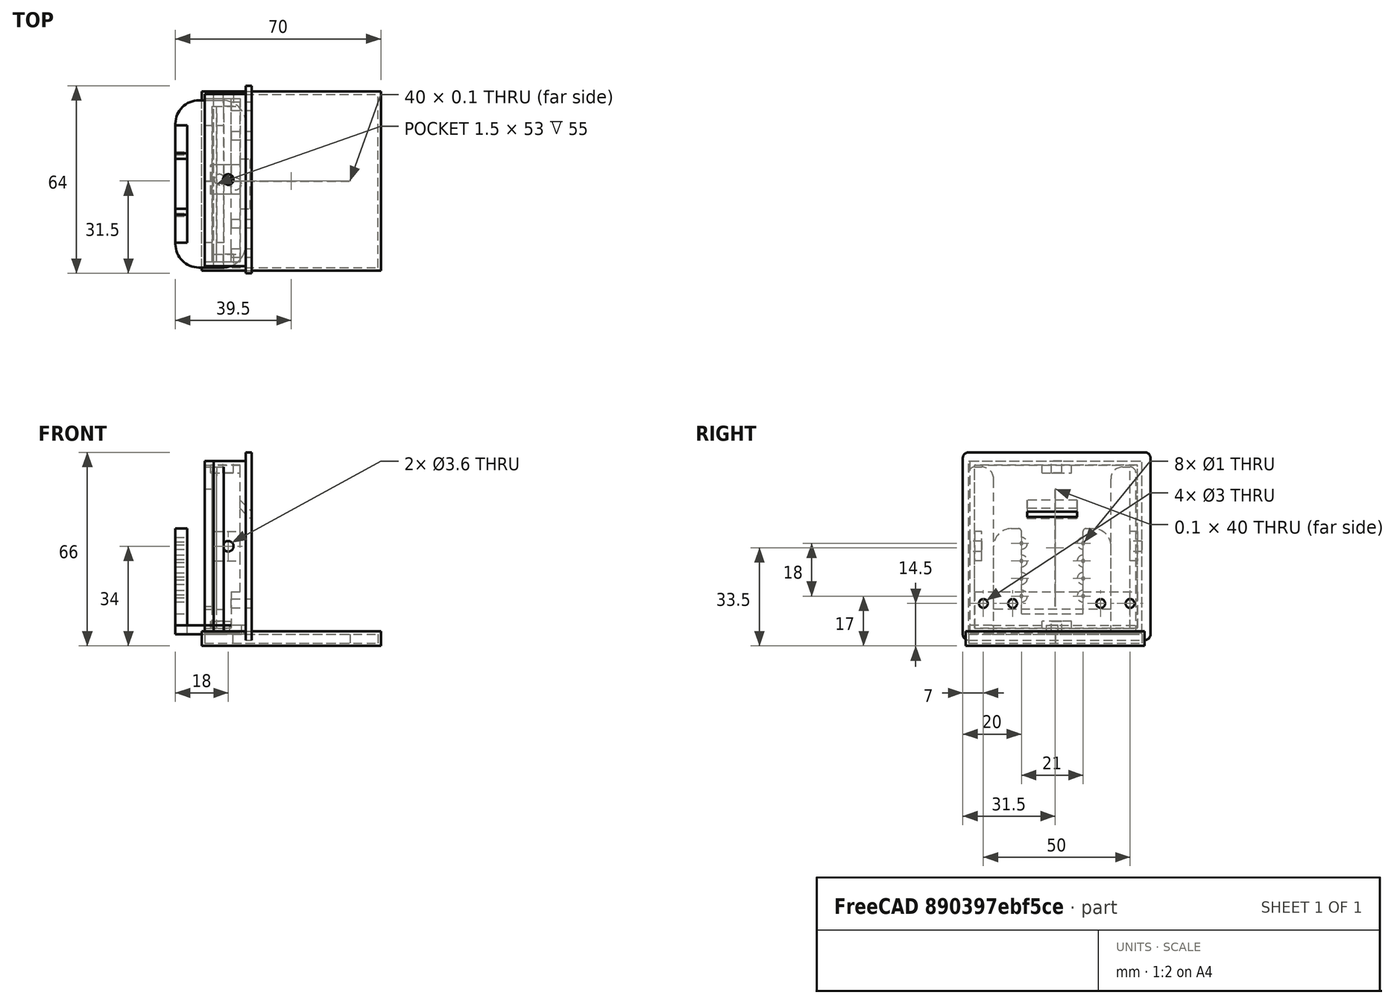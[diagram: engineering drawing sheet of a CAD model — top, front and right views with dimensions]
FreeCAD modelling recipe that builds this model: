
FCSTD DOCUMENT  (FreeCAD 0.18.4R)
Label: spectrometer
License: All rights reserved
LicenseURL: http://en.wikipedia.org/wiki/All_rights_reserved
objects: Part::Box×15, Part::FeaturePython×8, Part::Cylinder×7, Part::Cut×7, App::Part×6, Part::MultiFuse×6, Part::Fillet×6, Part::Feature×6, Path::FeaturePython×4, Spreadsheet::Sheet×1, Part::Compound×1, App::FeaturePython×1, App::DocumentObjectGroup×1, Path::FeatureCompoundPython×1, Part::Mirroring×1
note: 58 computed .brp shape members not serialized (recipe doc carries the construction recipe); baked Part::Feature solids carry a one-line shape summary decoded from their .brp

FEATURE [App::Part] Part  label="slide holder part"
  Origin = -> Origin
FEATURE [App::Part] Part001  label="rpi camera holder part"
  Origin = -> Origin001
FEATURE [Part::Cylinder] Cylinder  label="camera hole base"
  Angle = 360
  AttacherType = Attacher::AttachEngine3D
  Height = 4
  Placement = pos=(0,0,0) rot=(0,1,0;1.5708rad)
  Radius = 2
FEATURE [Part::FeaturePython] Array  label="camera hole base array"  # Draft array (typed FeaturePython)
  Angle = 360
  ArrayType = 0
  Axis = (0,0,1)
  Base = -> Cylinder
  Center = (0,0,0)
  Fuse = false
  IntervalAxis = (0,0,0)
  IntervalX = (1,0,0)
  IntervalY = (0,21,0)
  IntervalZ = (0,0,6)
  NumberPolar = 1
  NumberX = 1
  NumberY = 2
  NumberZ = 4
  Placement = pos=(0,7,2) rot=(0,0,1;0rad)
  expr: IntervalZ.z = p.camera_hole_dist_z / 2
  expr: IntervalY.y = p.camera_hole_dist_y
FEATURE [Spreadsheet::Sheet] Spreadsheet  label="p"
  cells = A1=camera_pcb_width; B1(camera_pcb_width)=25; A2=camera_pcb_height; B2(camera_pcb_height)=24; A3=camera_hole_dist_z; B3(camera_hole_dist_z)=12; A4=camera_hole_dist_y; B4(camera_hole_dist_y)=21; A5=slit_plate_width; B5(slit_plate_width)=59; A6=slit_plate_height; B6(slit_plate_height)=59; A7=slit_hole_height; B7(slit_hole_height)=40; A8=slit_hole_width; B8(slit_hole_width)=0.1
FEATURE [Part::Cylinder] Cylinder001  label="camera hole"
  Angle = 360
  AttacherType = Attacher::AttachEngine3D
  Height = 4
  Placement = pos=(0,0,0) rot=(0,1,0;1.5708rad)
  Radius = 0.5
FEATURE [Part::FeaturePython] Array001  label="camera hole array"  # Draft array (typed FeaturePython)
  Angle = 360
  ArrayType = 0
  Axis = (0,0,1)
  Base = -> Cylinder001
  Center = (0,0,0)
  Fuse = false
  IntervalAxis = (0,0,0)
  IntervalX = (1,0,0)
  IntervalY = (0,21,0)
  IntervalZ = (0,0,6)
  NumberPolar = 1
  NumberX = 1
  NumberY = 2
  NumberZ = 4
  Placement = pos=(0,7,2) rot=(0,0,1;0rad)
  expr: IntervalZ.z = p.camera_hole_dist_z / 2
  expr: IntervalY.y = p.camera_hole_dist_y
FEATURE [Part::Box] Box  label="camera plate"
  AttacherType = Attacher::AttachEngine3D
  Height = 36
  Length = 4
  Placement = pos=(0,-2.5,-11) rot=(0,0,1;0rad)
  Width = 40
FEATURE [Part::Box] Box001  label="camera plate hole"
  AttacherType = Attacher::AttachEngine3D
  Height = 74
  Length = 4
  Placement = pos=(0,7,-4) rot=(0,0,1;0rad)
  Width = 21
  expr: Height = p.camera_pcb_height + 50
  expr: Width = p.camera_pcb_width - 4
FEATURE [Part::Box] Box002  label="slide holder"
  AttacherType = Attacher::AttachEngine3D
  Height = 57
  Length = 6.5
  Width = 57
FEATURE [Part::Box] Box003  label="slide hole"
  AttacherType = Attacher::AttachEngine3D
  Height = 80
  Length = 1.5
  Placement = pos=(2.5,2,2) rot=(0,0,1;0rad)
  Width = 53
FEATURE [Part::Box] Box004  label="slide holder central hole"
  AttacherType = Attacher::AttachEngine3D
  Height = 100
  Length = 10
  Placement = pos=(-2,8.5,8.5) rot=(0,0,1;0rad)
  Width = 40
FEATURE [Part::MultiFuse] Fusion001  label="slide holder hole fusion"
  Shapes = -> [Box003,Box004]
FEATURE [Part::Box] Box005  label="bottom plate"
  AttacherType = Attacher::AttachEngine3D
  Height = 3
  Length = 24
  Placement = pos=(-10,0,0) rot=(0,0,1;0rad)
  Width = 57
FEATURE [Part::Cylinder] Cylinder002  label="central bottom hole"
  Angle = 360
  AttacherType = Attacher::AttachEngine3D
  Height = 10
  Placement = pos=(10.5,28.5,-4) rot=(0,0,1;0rad)
  Radius = 2
FEATURE [Part::Fillet] Fillet  label="bottom plate fillet"
  Base = -> Box005
  Edges = 4 edges r=8: [Edge1,Edge3,Edge5,Edge7]
FEATURE [Part::Cut] Cut003  label="bottom cut"
  Base = -> Fillet
  Tool = -> Cylinder002
FEATURE [Part::Fillet] Fillet001  label="camera plate fillet"
  Base = -> Box
  Edges = 2 edges r=6: [Edge10,Edge12]
FEATURE [Part::Cut] Cut001  label="camera plate cut"
  Base = -> Fillet001
  Tool = -> Box001
FEATURE [Part::Fillet] Fillet002  label="slide holder fillet"
  Base = -> Box002
  Edges = 2 edges r=2: [Edge10,Edge12]
FEATURE [Part::Cut] Cut002  label="slide holder cut"
  Base = -> Fillet002
  Tool = -> Fusion001
FEATURE [Part::Fillet] Fillet003  label="slider holder cut fillet"
  Base = -> Cut002
  Edges = 4 edges r=4: [Edge16,Edge23,Edge39,Edge49]
FEATURE [Part::Fillet] Fillet004  label="camera plate cut fillet"
  Base = -> Cut001
  Edges = 2 edges r=1: [Edge14,Edge21]
FEATURE [Part::MultiFuse] Fusion  label="camera plate fusion"
  Shapes = -> [Array,Fillet004]
FEATURE [Part::Cut] Cut  label="camera holder cut"
  Base = -> Fusion
  Placement = pos=(-10,11,11) rot=(0,0,1;0rad)
  Tool = -> Array001
FEATURE [Part::Compound] Compound  label="rpi camera slide holder"
  Links = -> [Cut003,Fillet003,Cut]
FEATURE [App::Part] Part002  label="bottom part"
  Group = -> [Box005,Cylinder002,Cut003,Fillet,Array,Compound,Fusion001,Fusion,Cut002,Cut,Cut001,Fillet002,Array001,Fillet001,Cylinder,Cylinder001,Box,Box001,Box002,Box003,Box004,Fillet003,Fillet004]
  Origin = -> Origin002
FEATURE [Part::Box] Box006  label="slit plate"
  AttacherType = Attacher::AttachEngine3D
  Height = 59
  Length = 3
  Width = 59
  expr: Height = p.slit_plate_height
  expr: Width = p.slit_plate_width
FEATURE [Part::Box] Box007  label="slit hole"
  AttacherType = Attacher::AttachEngine3D
  Height = 40
  Length = 10
  Placement = pos=(-3,29.45,9.5) rot=(0,0,1;0rad)
  Width = 0.1
  expr: Placement.Base.y = (p.slit_plate_width - p.slit_hole_width) / 2
  expr: Placement.Base.z = (p.slit_plate_height - p.slit_hole_height) / 2
  expr: Height = p.slit_hole_height
  expr: Width = p.slit_hole_width
FEATURE [Part::Cut] Cut004  label="slit plate cut"
  Base = -> Box006
  Tool = -> Box007
FEATURE [App::Part] Part003  label="slit part"
  Group = -> [Box006,Box007,Cut004]
  Origin = -> Origin003
  Placement = pos=(-125,-29,3) rot=(0,0,1;0rad)
FEATURE [Part::Feature] Cut004001  label="slit plate refine"
  Placement = pos=(0,0,0) rot=(0,1,0;1.5708rad)
  shape: bbox 59 x 59 x 3 mm, 10 faces (baked)
FEATURE [App::FeaturePython] SetupSheet  # Path/CAM operation (typed FeaturePython)
  ClearanceHeightExpression = OpStockZMax+SetupSheet.ClearanceHeightOffset
  ClearanceHeightOffset = 0
  FinalDepthExpression = OpFinalDepth
  HorizRapid = 100
  SafeHeightExpression = OpStockZMax+SetupSheet.SafeHeightOffset
  SafeHeightOffset = 0
  StartDepthExpression = OpStartDepth
  StepDownExpression = OpToolDiameter
  VertRapid = 100
FEATURE [Part::FeaturePython] Clone  label="Model-slit plate refine"  # Draft clone (typed FeaturePython)
  AttacherType = Attacher::AttachEngine3D
  Fuse = false
  Objects = -> [Cut004001]
  PathResource = Model
  Placement = pos=(0,0,0) rot=(0,1,0;1.5708rad)
  Scale = (1,1,1)
FEATURE [App::DocumentObjectGroup] Model
  Group = -> [Clone]
FEATURE [Path::FeaturePython] T3__laser  label="T3: laser"  # Path/CAM operation (typed FeaturePython)
  HorizFeed = 0.5
  HorizRapid = 100
  SpindleDir = 0
  SpindleSpeed = 1000
  ToolNumber = 3
  VertFeed = 0.5
  VertRapid = 100
  expr: VertRapid = SetupSheet.VertRapid
  expr: HorizRapid = SetupSheet.HorizRapid
FEATURE [Part::FeaturePython] Stock  # WARN: FeaturePython — macro-defined, semantics opaque (R4)
  Base = -> Model
  ExtXneg = 1
  ExtXpos = 1
  ExtYneg = 1
  ExtYpos = 1
  ExtZneg = 1
  ExtZpos = 1
  Placement = pos=(0,0,-3) rot=(0,0,1;0rad)
  StockType = FromBase
FEATURE [Path::FeaturePython] Engrave  # Path/CAM operation (typed FeaturePython)
  Active = true
  Base = -> [Clone]
  ClearanceHeight = 1
  FinalDepth = 0
  OpFinalDepth = -0.2
  OpStartDepth = 1.31e-14
  OpStockZMax = 1
  OpStockZMin = -4
  OpToolDiameter = 0.2
  SafeHeight = 1
  StartDepth = 0.1
  StartVertex = 0
  StepDown = 0.2
  ToolController = -> T3__laser
  expr: ClearanceHeight = OpStockZMax + SetupSheet.ClearanceHeightOffset
  expr: SafeHeight = OpStockZMax + SetupSheet.SafeHeightOffset
  expr: StepDown = OpToolDiameter
FEATURE [Path::FeaturePython] Contour  # Path/CAM operation (typed FeaturePython)
  Active = true
  AreaParams:
    Tolerance = 1e-07
    FitArcs = True
    Simplify = False
    CleanDistance = 0.0
    Accuracy = 0.01
    Unit = 1.0
    MinArcPoints = 4
    MaxArcPoints = 100
    ClipperScale = 10000000.0
    Fill = 0
    Coplanar = 2
    Reorient = True
    Outline = False
    Explode = False
    OpenMode = 0
    Deflection = 0.01
    SubjectFill = 0
    ClipFill = 0
    Offset = 0.1
    ExtraPass = 0
    Stepover = 0.0
    LastStepover = 0.0
    JoinType = 0
    EndType = 0
    MiterLimit = 2.0
    RoundPrecision = 0.0
    PocketMode = 0
    ToolRadius = 1.0
    PocketExtraOffset = 0.0
    PocketStepover = 0.0
    PocketLastStepover = 0.0
    FromCenter = False
    Angle = 45.0
    AngleShift = 0.0
    Shift = 0.0
    Thicken = False
    SectionCount = -1
    Stepdown = 1.0
    SectionOffset = 0.0
    SectionTolerance = 1e-06
    SectionMode = 2
    Project = False
  ClearanceHeight = 1
  Direction = 0
  FinalDepth = 0
  JoinType = 0
  MiterLimit = 0.1
  OffsetExtra = 0
  OpFinalDepth = -4
  OpStartDepth = 1
  OpStockZMax = 1
  OpStockZMin = -4
  OpToolDiameter = 0.2
  PathParams = {'orientation': 1, 'feedrate': 0.5, 'feedrate_v': 0.5, 'verbose': True, 'resume_height': 1.0000000000000133, 'retraction': 1.0000000000000133, 'return_end': True, 'preamble': False}
  SafeHeight = 1
  Side = 0
  StartDepth = 0.1
  StartPoint = (0,0,0)
  StepDown = 0.2
  ToolController = -> T3__laser
  UseComp = true
  UseStartPoint = false
  expr: ClearanceHeight = OpStockZMax + SetupSheet.ClearanceHeightOffset
  expr: SafeHeight = OpStockZMax + SetupSheet.SafeHeightOffset
  expr: StepDown = OpToolDiameter
FEATURE [Path::FeatureCompoundPython] Operations  # Path/CAM operation (typed FeaturePython)
  Group = -> [Engrave,Contour]
  UsePlacements = false
FEATURE [Path::FeaturePython] Job  label="slit plate job"  # Path/CAM operation (typed FeaturePython)
  GeometryTolerance = 0.01
  Model = -> Model
  Operations = -> Operations
  PostProcessor = 1
  PostProcessorOutputFile = <userpath>/work/roborep/freecad/spectrometer/slit_plate.gcode
  SetupSheet = -> SetupSheet
  Stock = -> Stock
  ToolController = -> [T3__laser]
FEATURE [Part::Box] Box008  label="outer wall"
  AttacherType = Attacher::AttachEngine3D
  Height = 58.6
  Length = 14
  Placement = pos=(0,0.5,0.5) rot=(0,0,1;0rad)
  Width = 58.6
FEATURE [Part::Feature] tube_block001
  Placement = pos=(14,30,-2) rot=(0,0,1;0rad)
  shape: bbox 127 x 64 x 62 mm, 1448 faces, 0 solids (baked)
FEATURE [Part::Cylinder] Cylinder003  label="horz hole"
  Angle = 360
  AttacherType = Attacher::AttachEngine3D
  Height = 80
  Placement = pos=(8,71,30) rot=(1,0,0;1.5708rad)
  Radius = 1.8
FEATURE [Part::Cylinder] Cylinder004  label="vert bottom hole"
  Angle = 360
  AttacherType = Attacher::AttachEngine3D
  Height = 40
  Placement = pos=(5,30,-12) rot=(1,0,0;0rad)
  Radius = 1.8
FEATURE [Part::Feature] tube_block_top001
  Placement = pos=(14,30,-2) rot=(0,0,1;0rad)
  shape: bbox 129.5 x 69 x 4 mm, 768 faces, 0 solids (baked)
FEATURE [Part::Cylinder] Cylinder005  label="vert top hole"
  Angle = 360
  AttacherType = Attacher::AttachEngine3D
  Height = 40
  Placement = pos=(8,30,40) rot=(1,0,0;0rad)
  Radius = 1.8
FEATURE [Part::Box] Box009  label="inner extraction"
  AttacherType = Attacher::AttachEngine3D
  Height = 55.6
  Length = 14
  Placement = pos=(-2,2,2) rot=(0,0,1;0rad)
  Width = 55.6
FEATURE [Part::Feature] raspberry_pi_bplus_bottom001
  shape: bbox 89.3 x 60.33 x 7.867 mm, 2032 faces, 0 solids (baked)
FEATURE [Part::Feature] raspberry_pi_bplus_top001
  shape: bbox 91.8 x 62.77 x 20.68 mm, 3224 faces, 0 solids (baked)
FEATURE [Part::Feature] rpi_box_holder001
  Placement = pos=(0,0,-5) rot=(0,0,1;0rad)
  shape: bbox 75 x 20 x 16 mm, 612 faces, 0 solids (baked)
FEATURE [Part::Mirroring] Part__Mirroring  label="rpi_box_holder001 (Mirror #1)"
  Base = (0,29.5,0)
  Normal = (0,1,0)
  Source = -> rpi_box_holder001
FEATURE [Part::Cylinder] Cylinder006  label="wall hole"
  Angle = 360
  AttacherType = Attacher::AttachEngine3D
  Height = 40
  Placement = pos=(-2.2e-15,5,10.5) rot=(0,1,0;1.5708rad)
  Radius = 1.5
FEATURE [Part::FeaturePython] Array002  label="wall hole array"  # Draft array (typed FeaturePython)
  Angle = 360
  ArrayType = 0
  Axis = (0,0,1)
  Base = -> Cylinder006
  Center = (0,0,0)
  Fuse = false
  IntervalAxis = (0,0,0)
  IntervalX = (1,0,0)
  IntervalY = (0,10,0)
  IntervalZ = (0,0,1)
  NumberPolar = 1
  NumberX = 1
  NumberY = 2
  NumberZ = 1
FEATURE [Part::FeaturePython] Array003  label="wall hole array array"  # Draft array (typed FeaturePython)
  Angle = 360
  ArrayType = 0
  Axis = (0,0,1)
  Base = -> Array002
  Center = (0,0,0)
  Fuse = false
  IntervalAxis = (0,0,0)
  IntervalX = (1,0,0)
  IntervalY = (0,40,0)
  IntervalZ = (0,0,1)
  NumberPolar = 1
  NumberX = 1
  NumberY = 2
  NumberZ = 1
  Placement = pos=(-10,0,0) rot=(0,0,1;0rad)
FEATURE [Part::Box] Box010  label="bottom addition"
  AttacherType = Attacher::AttachEngine3D
  Height = 14
  Length = 4
  Placement = pos=(9,0.5,0.5) rot=(0,0,1;0rad)
  Width = 58.6
FEATURE [Part::Box] Box011  label="camera cable hole"
  AttacherType = Attacher::AttachEngine3D
  Height = 2
  Length = 10
  Placement = pos=(8.41288,20,46.52) rot=(0,1,0;0.785398rad)
  Width = 17
FEATURE [Part::MultiFuse] Fusion002  label="back wall hole fusion"
  Shapes = -> [Box009,Box011]
FEATURE [App::Part] Part005  label="rpi box part"
  Group = -> [raspberry_pi_bplus_top001,raspberry_pi_bplus_bottom001]
  Origin = -> Origin005
  Placement = pos=(123,-5.5,4) rot=(0,0,1;3.14159rad)
FEATURE [Part::Box] Box012  label="back back wall"
  AttacherType = Attacher::AttachEngine3D
  Height = 64
  Length = 2
  Placement = pos=(14,-2,-2) rot=(0,0,1;0rad)
  Width = 64
FEATURE [Part::Fillet] Fillet005  label="back back wall fillet"
  Base = -> Box012
  Edges = 4 edges r=2: [Edge9,Edge10,Edge11,Edge12]
FEATURE [Part::MultiFuse] Fusion004  label="back outer wall fusion"
  Shapes = -> [Box008,Fillet005]
FEATURE [Part::Cut] Cut004002  label="back wall cut"
  Base = -> Fusion004
  Tool = -> Fusion002
FEATURE [Part::Box] Box013  label="enforcers"
  AttacherType = Attacher::AttachEngine3D
  Height = 4
  Length = 10
  Placement = pos=(2,25,0.5) rot=(0,0,1;0rad)
  Width = 10
FEATURE [Part::FeaturePython] Array004  label="enf array"  # Draft array (typed FeaturePython)
  Angle = 360
  ArrayType = 0
  Axis = (0,0,1)
  Base = -> Box013
  Center = (0,0,0)
  Fuse = false
  IntervalAxis = (0,0,0)
  IntervalX = (1,0,0)
  IntervalY = (0,1,0)
  IntervalZ = (0,0,54.5)
  NumberPolar = 1
  NumberX = 1
  NumberY = 1
  NumberZ = 2
FEATURE [Part::MultiFuse] Fusion005  label="around wall hole fusion"
  Shapes = -> [Cylinder003,Cylinder004,Cylinder005,Array003]
FEATURE [Part::Box] Box014  label="enforcers001"
  AttacherType = Attacher::AttachEngine3D
  Height = 10
  Length = 10
  Placement = pos=(3,0.5,25) rot=(0,0,1;0rad)
  Width = 4
FEATURE [Part::FeaturePython] Array005  label="enf array001"  # Draft array (typed FeaturePython)
  Angle = 360
  ArrayType = 0
  Axis = (0,0,1)
  Base = -> Box014
  Center = (0,0,0)
  Fuse = false
  IntervalAxis = (0,0,0)
  IntervalX = (1,0,0)
  IntervalY = (0,54.5,0)
  IntervalZ = (0,0,1)
  NumberPolar = 1
  NumberX = 1
  NumberY = 2
  NumberZ = 1
FEATURE [Part::MultiFuse] Fusion003  label="outer wall cut fusion"
  Shapes = -> [Cut004002,Box010,Array004,Array005]
FEATURE [Part::Cut] Cut004003  label="back wall whole cut"
  Base = -> Fusion003
  Tool = -> Fusion005
FEATURE [App::Part] Part004  label="back rpi holder wall part"
  Group = -> [Box008,Cylinder003,Cylinder004,Cylinder005,Box009,Fusion002,Cut004002,Cylinder006,Array002,Array003,Box010,Fusion003,Cut004003,Box011,Box012,Fusion004,Fillet005,Box013,Array004,Fusion005,Box014,Array005]
  Origin = -> Origin004
